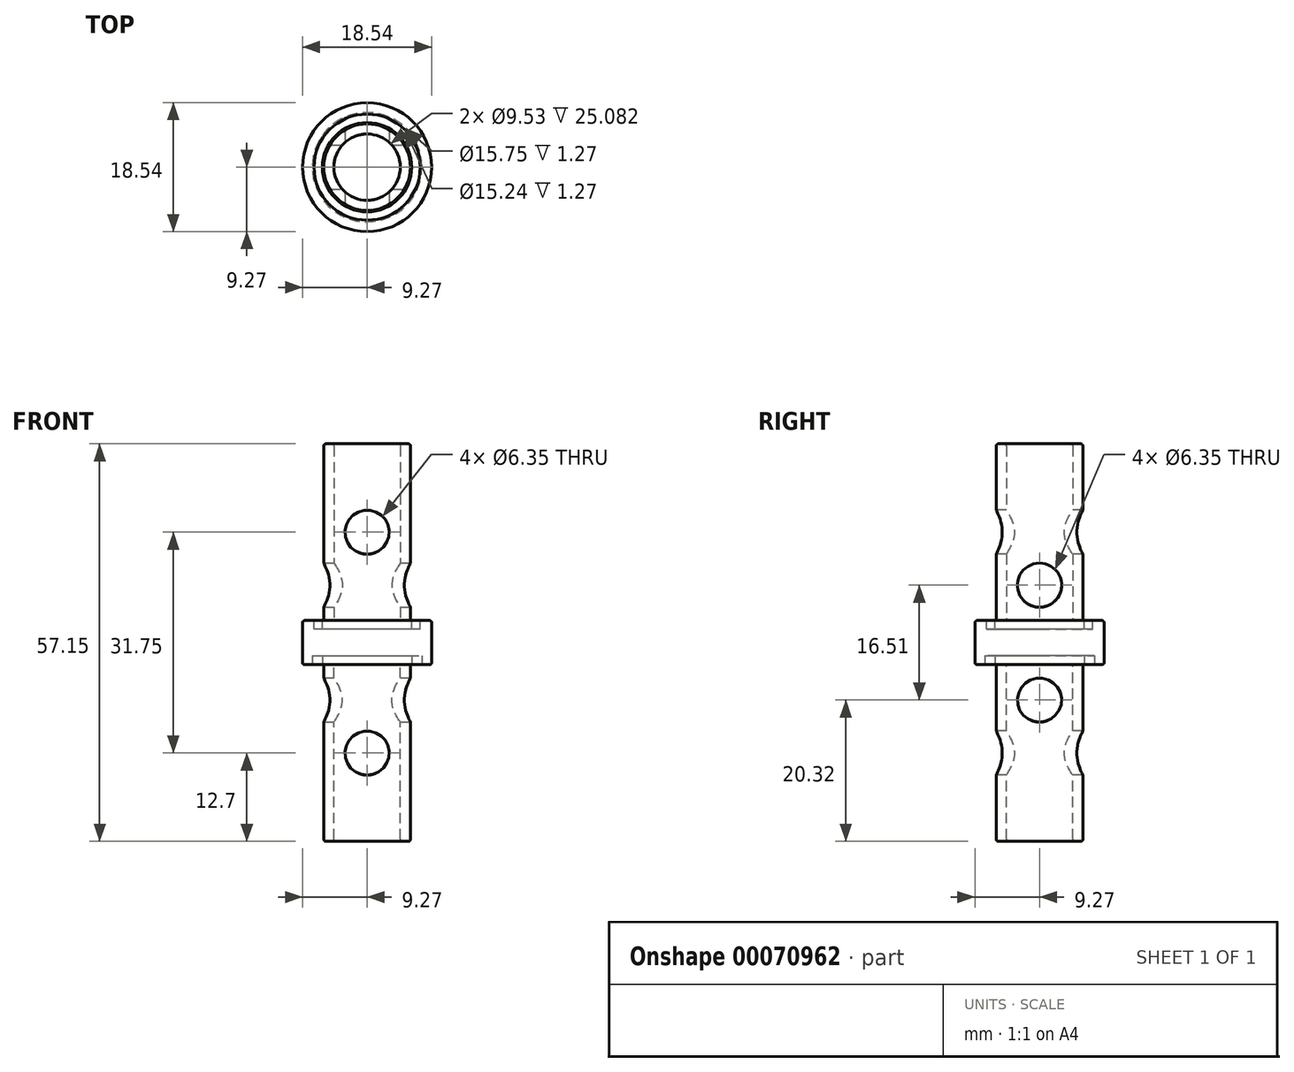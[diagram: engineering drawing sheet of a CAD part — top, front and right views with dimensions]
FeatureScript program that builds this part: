
annotation { "Feature Type Name" : "Feature", "Feature Type Description" : "" }
export const myFeature = defineFeature(function(context is Context, id is Id, definition is map)
    precondition{}
    {
        {
            var Q0;
            Q0=qCreatedBy(makeId("Top.planeOp"),FACE);
            var sketch = newSketch(context, id + "F0", { "sketchPlane" : qUnion([Q0])});
            skCircle(sketch, "E0", {"center": v(0, 0) * mm, "radius": 9.27 * mm});
            skSolve(sketch);
        }
        {
            var Q0;
            Q0 = qSketchRegion(id + "F0", true);
            extrude(context, id + "F1", {"entities" : qUnion([Q0]), "depth" : 6.35 * mm});
        }
        {
            var Q0;
            Q0=makeQuery(id+"F1.opExtrude","CAP_FACE",FACE,{"disambiguationData":[OSD([sQuery(id+"F0.wireOp",EDGE,"E0")])],"isStart":false});
            var sketch = newSketch(context, id + "F2", { "sketchPlane" : qUnion([Q0])});
            skCircle(sketch, "E1", {"center": v(0, 0) * mm, "radius": 6.22 * mm});
            skCircle(sketch, "E2", {"center": v(0, 0) * mm, "radius": 4.76 * mm});
            skSolve(sketch);
        }
        {
            var Q0;
            Q0 = qSketchRegion(id + "F2", true);
            extrude(context, id + "F3", {"entities" : qUnion([Q0]), "operationType" : NewBodyOperationType.ADD, "depth" : 25.4 * mm});
        }
        {
            var Q0;
            Q0=makeQuery(id+"F1.opExtrude","CAP_FACE",FACE,{"disambiguationData":[OSD([sQuery(id+"F0.wireOp",EDGE,"E0")])],"isStart":true});
            var sketch = newSketch(context, id + "F4", { "sketchPlane" : qUnion([Q0])});
            skCircle(sketch, "E3", {"center": v(0, 0) * mm, "radius": 6.22 * mm});
            skCircle(sketch, "E4", {"center": v(0, 0) * mm, "radius": 4.76 * mm});
            skSolve(sketch);
        }
        {
            var Q0;
            Q0 = qSketchRegion(id + "F4", true);
            extrude(context, id + "F5", {"entities" : qUnion([Q0]), "operationType" : NewBodyOperationType.ADD, "depth" : 25.4 * mm});
        }
        {
            var Q0;
            Q0=qCreatedBy(makeId("Right.planeOp"),FACE);
            var sketch = newSketch(context, id + "F6", { "sketchPlane" : qUnion([Q0])});
            skCircle(sketch, "E5", {"center": v(0, -5.08) * mm, "radius": 3.18 * mm});
            skCircle(sketch, "E6", {"center": v(0, 11.43) * mm, "radius": 3.18 * mm});
            skSolve(sketch);
        }
        {
            var Q0;
            Q0 = qSketchRegion(id + "F6", true);
            extrude(context, id + "F7", {"entities" : qUnion([Q0]), "operationType" : NewBodyOperationType.REMOVE, "endBound" : BoundingType.SYMMETRIC, "oppositeDirection" : true, "depth" : 25.4 * mm});
        }
        {
            var Q0;
            Q0=qCreatedBy(makeId("Front.planeOp"),FACE);
            var sketch = newSketch(context, id + "F8", { "sketchPlane" : qUnion([Q0])});
            skCircle(sketch, "E7", {"center": v(0, -12.7) * mm, "radius": 3.17 * mm});
            skCircle(sketch, "E8", {"center": v(0, 19.05) * mm, "radius": 3.18 * mm});
            skSolve(sketch);
        }
        {
            var Q0;
            Q0 = qSketchRegion(id + "F8", true);
            extrude(context, id + "F9", {"entities" : qUnion([Q0]), "operationType" : NewBodyOperationType.REMOVE, "endBound" : BoundingType.SYMMETRIC, "oppositeDirection" : true, "depth" : 25.4 * mm});
        }
        {
            var Q0;
            {var subQ0=sQuery(id+"F0.wireOp",EDGE,"E0");Q0=makeQuery(id+"F5.boolean.opBoolean","SPLIT",FACE,{"disambiguationData":[TD([makeQuery(id+"F1.opExtrude","SWEPT_FACE",FACE,{"disambiguationData":[OSD([subQ0])]})])],"derivedFrom":makeQuery(id+"F1.opExtrude","CAP_FACE",FACE,{"disambiguationData":[OSD([subQ0])],"isStart":true})});}
            var sketch = newSketch(context, id + "F10", { "sketchPlane" : qUnion([Q0])});
            skCircle(sketch, "E9", {"center": v(0, 0) * mm, "radius": 6.41 * mm});
            skCircle(sketch, "E10", {"center": v(0, 0) * mm, "radius": 7.87 * mm});
            skSolve(sketch);
        }
        {
            var Q0;
            Q0 = qSketchRegion(id + "F10", true);
            extrude(context, id + "F11", {"entities" : qUnion([Q0]), "operationType" : NewBodyOperationType.REMOVE, "oppositeDirection" : true, "depth" : 1.27 * mm});
        }
        {
            var Q0;
            {var subQ0=sQuery(id+"F0.wireOp",EDGE,"E0");Q0=makeQuery(id+"F3.boolean.opBoolean","SPLIT",FACE,{"disambiguationData":[TD([makeQuery(id+"F1.opExtrude","SWEPT_FACE",FACE,{"disambiguationData":[OSD([subQ0])]})])],"derivedFrom":makeQuery(id+"F1.opExtrude","CAP_FACE",FACE,{"disambiguationData":[OSD([subQ0])],"isStart":false})});}
            var sketch = newSketch(context, id + "F12", { "sketchPlane" : qUnion([Q0])});
            skCircle(sketch, "E11", {"center": v(0, 0) * mm, "radius": 7.62 * mm});
            skCircle(sketch, "E12", {"center": v(0, 0) * mm, "radius": 6.41 * mm});
            skSolve(sketch);
        }
        {
            var Q0;
            Q0 = qSketchRegion(id + "F12", true);
            extrude(context, id + "F13", {"entities" : qUnion([Q0]), "operationType" : NewBodyOperationType.REMOVE, "oppositeDirection" : true, "depth" : 1.27 * mm});
        }
        {
            var Q0;
            Q0=makeQuery(id+"F1.opExtrude","CAP_EDGE",EDGE,{"disambiguationData":[OSD([sQuery(id+"F0.wireOp",EDGE,"E0")])],"isStart":false});
            var Q1;
            Q1=makeQuery(id+"F3.opExtrude","CAP_EDGE",EDGE,{"disambiguationData":[OSD([sQuery(id+"F2.wireOp",EDGE,"E1")])],"isStart":false});
            var Q2;
            Q2=makeQuery(id+"F1.opExtrude","CAP_EDGE",EDGE,{"disambiguationData":[OSD([sQuery(id+"F0.wireOp",EDGE,"E0")])],"isStart":true});
            var Q3;
            Q3=makeQuery(id+"F5.opExtrude","CAP_EDGE",EDGE,{"disambiguationData":[OSD([sQuery(id+"F4.wireOp",EDGE,"E3")])],"isStart":false});
            var Q4;
            Q4=makeQuery(id+"F5.opExtrude","CAP_EDGE",EDGE,{"disambiguationData":[OSD([sQuery(id+"F4.wireOp",EDGE,"E4")])],"isStart":false});
            var Q5;
            Q5=makeQuery(id+"F3.opExtrude","CAP_EDGE",EDGE,{"disambiguationData":[OSD([sQuery(id+"F2.wireOp",EDGE,"E2")])],"isStart":false});
            fillet(context, id + "F14", {"entities" : qUnion([Q0, Q1, Q2, Q3, Q4, Q5]), "radius" : 0.32 * mm, "tangentPropagation" : true, "allowEdgeOverflow" : false});
        }
    });
